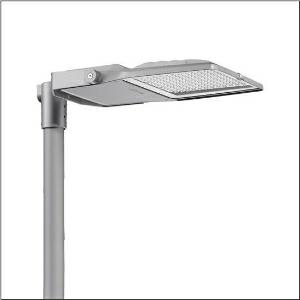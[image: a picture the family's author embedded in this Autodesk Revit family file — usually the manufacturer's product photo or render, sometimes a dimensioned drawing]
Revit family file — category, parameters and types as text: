
# Revit family: floodlight_fl_21_midi___pl43_5xa7781e2a3a_9ccb
name_source: partatom
category: Lighting Fixtures
units: mm (PartAtom-declared; Revit-internal decimal feet)

## family parameters
Cut with Voids When Loaded = No
Host = Face
Light Source = No
Part Type = Normal
Room Calculation Point = No
Round Connector Dimension = Use Diameter
Shared = No

## types (1)
- --- (1 x LED, 27540 lm, 208.1 W, 3000K)
    Apparent Load = 208 VA
    CIE Flux Codes = 27 78 99 100 100
    Color Rendering = 70
    Color Temperature = 3000K
    Default Elevation = 1800 mm
    Description = Floodlight FL 21 midi, floodlight, primary light control with lens, of PMMA, primary optical cover: protective disc, of toughened safety glass, transparent, light distribution: PL43, light emission: direct distribution, installation type: surface-mounted, LED, High Power LED, rated luminous flux: 27.540lm, luminous efficacy: 132lm/W, light colour: 730, colour temperature: 3000K, control gear: ECG iQ, control: optimised constant luminous flux control (CLO 2.0), Desk-Remote (wireless, voltage-free reading and setting of iQ features in the workshop via application-optimized NFC function/RFID function), Light-Fading, Smart-Wire, Night-Set, Lumen-Switch, Temp-Guard, Auto-Match, with terminal, 6-pole, mains connection: 220..240V, AC, 50/60Hz, start of lifetime: 208W, end of lifetime: 227W, reduction: 90W, luminaire housing, of diecast aluminium, powder-coated, Siteco® metallic grey (DB 702S), corrosivity category C5 according to DIN EN ISO 12944, mast bracket, of steel, galvanised, powder-coated, Siteco® metallic grey (DB 702S), protection rating (complete): IP66, insulation class (complete): insulation class I (protective earthing), certification: CE, protection symbol: D, impact resistance: IK08, permissible operating ambient temperature: -40..+40°C, permissible operating ambient temperature for outdoor applications: -40..+50°C, standard: DIN EN 12944, packaging unit: 1 piece

Light Distribution: PL43
    Height = 76 mm
    Lamp = 1 x LED
    Lamp Light Flux = 27540 lm
    Lamp Power = 208.1 W
    Lamp count = 1
    Length = 657 mm
    Luminous efficacy = 132 lm/W
    Manufacturer = Siteco
    ModVariant = No
    Model = 5XA7781E2A3A
    Number of Poles = 1
    OnlyDefault = Yes
    Power Factor = 1
    Product Name = Floodlight FL 21 midi | PL43
    Product group = floodlight | pylon top
    ProductGroupID = 6101
    Protection Class = Protection class I
    Protection Degree = IP 66
    RLX_Detail_Level = 1
    RlxData = <blob elided: 153369 chars, md5=2d909659>
    Socket = socket
    Standby Power = 0 W
    System Light Flux = 27540 lm
    System Power = 208 W
    Type Comments = factory setting: luminous flux: 100 % | dim-lin: 254 | 710 mA
    Type Image = l_1007123.jpg
    URL = http://relux.com
    VarID = @adj_013981
    Voltage = 0 V
    Weight = 0.00 kg
    Width = 442 mm

## geometry (parser evidence)
native form markers: Blend x4, Sweep x15
no freeform markers — native parametric forms only
